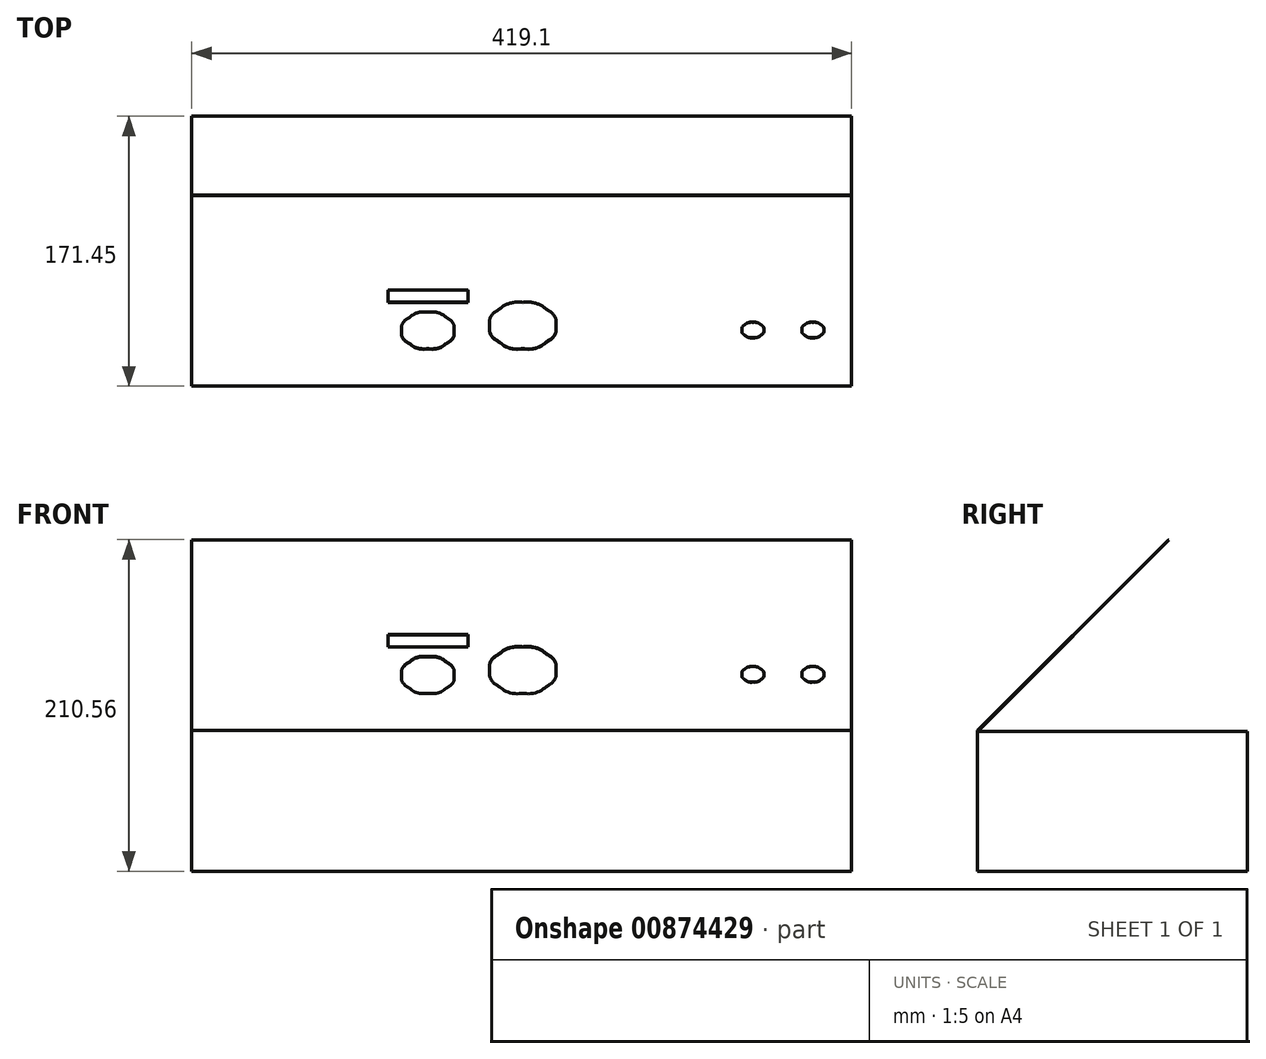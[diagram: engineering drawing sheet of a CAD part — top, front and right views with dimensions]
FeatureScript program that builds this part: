
annotation { "Feature Type Name" : "Feature", "Feature Type Description" : "" }
export const myFeature = defineFeature(function(context is Context, id is Id, definition is map)
    precondition{}
    {
        {
            var Q0;
            Q0=qCreatedBy(makeId("Right.planeOp"),FACE);
            var sketch = newSketch(context, id + "F0", { "sketchPlane" : qUnion([Q0])});
            skLineSegment(sketch, "E0.bottom", {"start": v(0, 0) * mm, "end": v(-171.45, 0) * mm});
            skLineSegment(sketch, "E0.top", {"start": v(0, 88.9) * mm, "end": v(-171.04, 88.9) * mm});
            skLineSegment(sketch, "E0.left", {"start": v(0, 0) * mm, "end": v(0, 88.9) * mm});
            skLineSegment(sketch, "E0.right", {"start": v(-171.45, 0) * mm, "end": v(-171.45, 89.32) * mm});
            skLineSegment(sketch, "E1", {"start": v(-171.45, 89.32) * mm, "end": v(-50.22, 210.56) * mm});
            skLineSegment(sketch, "E2", {"start": v(-50.22, 210.56) * mm, "end": v(-49.93, 210.27) * mm});
            skLineSegment(sketch, "E3", {"start": v(-49.93, 210.27) * mm, "end": v(-171.04, 89.15) * mm});
            skLineSegment(sketch, "E4", {"start": v(-171.04, 88.9) * mm, "end": v(-171.04, 89.15) * mm});
            skLineSegment(sketch, "E5", {"start": v(-171.04, 88.9) * mm, "end": v(-171.45, 88.9) * mm, "construction": true});
            skSolve(sketch);
        }
        {
            var Q0;
            Q0=qSketchRegion(id+"F0",true);
            extrude(context, id + "F1", {"entities" : qUnion([Q0]), "endBound" : BoundingType.SYMMETRIC, "depth" : 419.1 * mm, "offsetDistance" : 25.4 * mm});
        }
        {
            var Q0;
            Q0=makeQuery(id+"F1.opExtrude","SWEPT_FACE",FACE,{"disambiguationData":[OSD([sQuery(id+"F0.wireOp",EDGE,"E1")])]});
            var sketch = newSketch(context, id + "F2", { "sketchPlane" : qUnion([Q0])});
            skLineSegment(sketch, "E6", {"start": v(69.53, 16.47) * mm, "end": v(69.53, -24.8) * mm});
            skLineSegment(sketch, "E7", {"start": v(90.57, -24.8) * mm, "end": v(90.57, 16.47) * mm});
            skLineSegment(sketch, "E8", {"start": v(90.57, 16.47) * mm, "end": v(69.53, 16.47) * mm});
            skLineSegment(sketch, "E9", {"start": v(90.57, -24.8) * mm, "end": v(69.53, -24.8) * mm});
            skLineSegment(sketch, "E10", {"start": v(-84.97, 28.38) * mm, "end": v(-84.97, 17.27) * mm});
            skLineSegment(sketch, "E11", {"start": v(-34.17, 17.27) * mm, "end": v(-34.17, 28.38) * mm});
            skLineSegment(sketch, "E12", {"start": v(-34.17, 28.38) * mm, "end": v(-84.97, 28.38) * mm});
            skLineSegment(sketch, "E13", {"start": v(-84.97, 17.27) * mm, "end": v(-34.17, 17.27) * mm});
            skLineSegment(sketch, "E14", {"start": v(162.89, 112.52) * mm, "end": v(160.64, 112.52) * mm});
            skLineSegment(sketch, "E15", {"start": v(-208.87, -56.95) * mm, "end": v(210.23, -56.95) * mm, "construction": true});
            skLineSegment(sketch, "E16", {"start": v(-208.87, 112.52) * mm, "end": v(210.23, 112.52) * mm, "construction": true});
            skLineSegment(sketch, "E17", {"start": v(-208.81, -57.03) * mm, "end": v(-208.81, 112.44) * mm, "construction": true});
            skLineSegment(sketch, "E18", {"start": v(210.29, -57.03) * mm, "end": v(210.29, 112.44) * mm, "construction": true});
            skFitSpline(sketch, "E19", {"points": [v(-59.65, 8.54) * mm, v(-64.01, 8.54) * mm, v(-68.35, 6.74) * mm, v(-71.43, 3.65) * mm]});
            skFitSpline(sketch, "E20", {"points": [v(-71.43, 3.65) * mm, v(-74.52, 0.57) * mm, v(-76.32, -3.77) * mm, v(-76.32, -8.13) * mm, v(-76.32, -12.5) * mm, v(-74.52, -16.83) * mm, v(-71.43, -19.92) * mm]});
            skFitSpline(sketch, "E21", {"points": [v(-71.43, -19.92) * mm, v(-68.35, -23) * mm, v(-64.01, -24.8) * mm, v(-59.65, -24.8) * mm, v(-55.28, -24.8) * mm, v(-50.95, -23) * mm, v(-47.86, -19.92) * mm]});
            skFitSpline(sketch, "E22", {"points": [v(-47.86, -19.92) * mm, v(-44.78, -16.83) * mm, v(-42.98, -12.5) * mm, v(-42.98, -8.13) * mm, v(-42.98, -3.77) * mm, v(-44.78, 0.57) * mm, v(-47.86, 3.65) * mm]});
            skFitSpline(sketch, "E23", {"points": [v(-47.86, 3.65) * mm, v(-50.95, 6.74) * mm, v(-55.28, 8.54) * mm, v(-59.65, 8.54) * mm]});
            skFitSpline(sketch, "E24", {"points": [v(0.68, 17.27) * mm, v(-4.83, 17.27) * mm, v(-10.3, 15) * mm, v(-14.2, 11.1) * mm]});
            skFitSpline(sketch, "E25", {"points": [v(-14.2, 11.1) * mm, v(-18.1, 7.21) * mm, v(-20.36, 1.74) * mm, v(-20.36, -3.77) * mm, v(-20.36, -9.27) * mm, v(-18.1, -14.75) * mm, v(-14.2, -18.64) * mm]});
            skFitSpline(sketch, "E26", {"points": [v(-14.2, -18.64) * mm, v(-10.3, -22.54) * mm, v(-4.83, -24.8) * mm, v(0.68, -24.8) * mm, v(6.18, -24.8) * mm, v(11.66, -22.54) * mm, v(15.55, -18.64) * mm]});
            skFitSpline(sketch, "E27", {"points": [v(15.55, -18.64) * mm, v(19.44, -14.75) * mm, v(21.71, -9.27) * mm, v(21.71, -3.77) * mm, v(21.71, 1.74) * mm, v(19.44, 7.21) * mm, v(15.55, 11.1) * mm]});
            skFitSpline(sketch, "E28", {"points": [v(15.55, 11.1) * mm, v(11.66, 15) * mm, v(6.18, 17.27) * mm, v(0.68, 17.27) * mm]});
            skFitSpline(sketch, "E29", {"points": [v(146.73, -0.6) * mm, v(144.9, -0.6) * mm, v(143.1, -1.34) * mm, v(141.82, -2.63) * mm]});
            skFitSpline(sketch, "E30", {"points": [v(141.82, -2.63) * mm, v(140.53, -3.91) * mm, v(139.78, -5.72) * mm, v(139.78, -7.54) * mm, v(139.78, -9.36) * mm, v(140.53, -11.16) * mm, v(141.82, -12.45) * mm]});
            skFitSpline(sketch, "E31", {"points": [v(141.82, -12.45) * mm, v(143.1, -13.73) * mm, v(144.9, -14.48) * mm, v(146.73, -14.48) * mm, v(148.55, -14.48) * mm, v(150.35, -13.73) * mm, v(151.64, -12.45) * mm]});
            skFitSpline(sketch, "E32", {"points": [v(151.64, -12.45) * mm, v(152.92, -11.16) * mm, v(153.67, -9.36) * mm, v(153.67, -7.54) * mm, v(153.67, -5.72) * mm, v(152.92, -3.91) * mm, v(151.64, -2.63) * mm]});
            skFitSpline(sketch, "E33", {"points": [v(151.64, -2.63) * mm, v(150.35, -1.34) * mm, v(148.55, -0.6) * mm, v(146.73, -0.6) * mm]});
            skFitSpline(sketch, "E34", {"points": [v(184.83, -0.6) * mm, v(183, -0.6) * mm, v(181.2, -1.34) * mm, v(179.92, -2.63) * mm]});
            skFitSpline(sketch, "E35", {"points": [v(179.92, -2.63) * mm, v(178.63, -3.91) * mm, v(177.88, -5.72) * mm, v(177.88, -7.54) * mm, v(177.88, -9.36) * mm, v(178.63, -11.16) * mm, v(179.92, -12.45) * mm]});
            skFitSpline(sketch, "E36", {"points": [v(179.92, -12.45) * mm, v(181.2, -13.73) * mm, v(183, -14.48) * mm, v(184.83, -14.48) * mm, v(186.65, -14.48) * mm, v(188.45, -13.73) * mm, v(189.74, -12.45) * mm]});
            skFitSpline(sketch, "E37", {"points": [v(189.74, -12.45) * mm, v(191.02, -11.16) * mm, v(191.77, -9.36) * mm, v(191.77, -7.54) * mm, v(191.77, -5.72) * mm, v(191.02, -3.91) * mm, v(189.74, -2.63) * mm]});
            skFitSpline(sketch, "E38", {"points": [v(189.74, -2.63) * mm, v(188.45, -1.34) * mm, v(186.65, -0.6) * mm, v(184.83, -0.6) * mm]});
            skFitSpline(sketch, "E39", {"points": [v(146.79, -0.67) * mm, v(144.97, -0.67) * mm, v(143.16, -1.42) * mm, v(141.88, -2.7) * mm]});
            skFitSpline(sketch, "E40", {"points": [v(141.88, -2.7) * mm, v(140.59, -4) * mm, v(139.84, -5.8) * mm, v(139.84, -7.62) * mm, v(139.84, -9.43) * mm, v(140.59, -11.24) * mm, v(141.88, -12.53) * mm]});
            skFitSpline(sketch, "E41", {"points": [v(141.88, -12.53) * mm, v(143.16, -13.81) * mm, v(144.97, -14.56) * mm, v(146.79, -14.56) * mm, v(148.6, -14.56) * mm, v(150.41, -13.81) * mm, v(151.7, -12.53) * mm, v(152.98, -11.24) * mm, v(153.73, -9.43) * mm, v(153.73, -7.62) * mm, v(153.73, -5.8) * mm, v(152.98, -4) * mm, v(151.7, -2.7) * mm]});
            skFitSpline(sketch, "E42", {"points": [v(151.7, -2.7) * mm, v(150.41, -1.42) * mm, v(148.6, -0.67) * mm, v(146.79, -0.67) * mm]});
            skFitSpline(sketch, "E43", {"points": [v(184.89, -0.67) * mm, v(183.07, -0.67) * mm, v(181.26, -1.42) * mm, v(179.98, -2.7) * mm]});
            skFitSpline(sketch, "E44", {"points": [v(179.98, -2.7) * mm, v(178.69, -4) * mm, v(177.94, -5.8) * mm, v(177.94, -7.62) * mm, v(177.94, -9.43) * mm, v(178.69, -11.24) * mm, v(179.98, -12.53) * mm]});
            skFitSpline(sketch, "E45", {"points": [v(179.98, -12.53) * mm, v(181.26, -13.81) * mm, v(183.07, -14.56) * mm, v(184.89, -14.56) * mm, v(186.7, -14.56) * mm, v(188.51, -13.81) * mm, v(189.8, -12.53) * mm, v(191.08, -11.24) * mm, v(191.83, -9.43) * mm, v(191.83, -7.62) * mm, v(191.83, -5.8) * mm, v(191.08, -4) * mm, v(189.8, -2.7) * mm]});
            skFitSpline(sketch, "E46", {"points": [v(189.8, -2.7) * mm, v(188.51, -1.42) * mm, v(186.7, -0.67) * mm, v(184.89, -0.67) * mm]});
            skFitSpline(sketch, "E47", {"points": [v(146.73, -0.6) * mm, v(144.9, -0.6) * mm, v(143.1, -1.34) * mm, v(141.82, -2.63) * mm]});
            skFitSpline(sketch, "E48", {"points": [v(141.82, -2.63) * mm, v(140.53, -3.91) * mm, v(139.78, -5.72) * mm, v(139.78, -7.54) * mm, v(139.78, -9.36) * mm, v(140.53, -11.16) * mm, v(141.82, -12.45) * mm]});
            skFitSpline(sketch, "E49", {"points": [v(141.82, -12.45) * mm, v(143.1, -13.74) * mm, v(144.9, -14.48) * mm, v(146.73, -14.48) * mm, v(148.54, -14.48) * mm, v(150.35, -13.74) * mm, v(151.64, -12.45) * mm]});
            skFitSpline(sketch, "E50", {"points": [v(151.64, -12.45) * mm, v(152.92, -11.16) * mm, v(153.67, -9.36) * mm, v(153.67, -7.54) * mm, v(153.67, -5.72) * mm, v(152.92, -3.91) * mm, v(151.64, -2.63) * mm]});
            skFitSpline(sketch, "E51", {"points": [v(151.64, -2.63) * mm, v(150.35, -1.34) * mm, v(148.54, -0.6) * mm, v(146.73, -0.6) * mm]});
            skFitSpline(sketch, "E52", {"points": [v(184.83, -0.6) * mm, v(183, -0.6) * mm, v(181.2, -1.34) * mm, v(179.92, -2.63) * mm]});
            skFitSpline(sketch, "E53", {"points": [v(179.92, -2.63) * mm, v(178.63, -3.91) * mm, v(177.88, -5.72) * mm, v(177.88, -7.54) * mm, v(177.88, -9.36) * mm, v(178.63, -11.16) * mm, v(179.92, -12.45) * mm]});
            skFitSpline(sketch, "E54", {"points": [v(179.92, -12.45) * mm, v(181.2, -13.74) * mm, v(183, -14.48) * mm, v(184.83, -14.48) * mm, v(186.64, -14.48) * mm, v(188.45, -13.74) * mm, v(189.74, -12.45) * mm]});
            skFitSpline(sketch, "E55", {"points": [v(189.74, -12.45) * mm, v(191.02, -11.16) * mm, v(191.77, -9.36) * mm, v(191.77, -7.54) * mm, v(191.77, -5.72) * mm, v(191.02, -3.91) * mm, v(189.74, -2.63) * mm]});
            skFitSpline(sketch, "E56", {"points": [v(189.74, -2.63) * mm, v(188.45, -1.34) * mm, v(186.64, -0.6) * mm, v(184.83, -0.6) * mm]});
            skSolve(sketch);
        }
        {
            var Q0;
            Q0=qSketchRegion(id+"F2",true);
            var Q1;
            Q1=makeQuery(id+"F1.opExtrude","SWEPT_FACE",FACE,{"disambiguationData":[OSD([sQuery(id+"F0.wireOp",EDGE,"E3")])]});
            extrude(context, id + "F3", {"entities" : qUnion([Q0]), "operationType" : NewBodyOperationType.REMOVE, "endBound" : BoundingType.UP_TO_SURFACE, "oppositeDirection" : true, "depth" : 25.4 * mm, "endBoundEntityFace" : qUnion([Q1]), "offsetDistance" : 25.4 * mm});
        }
    });
